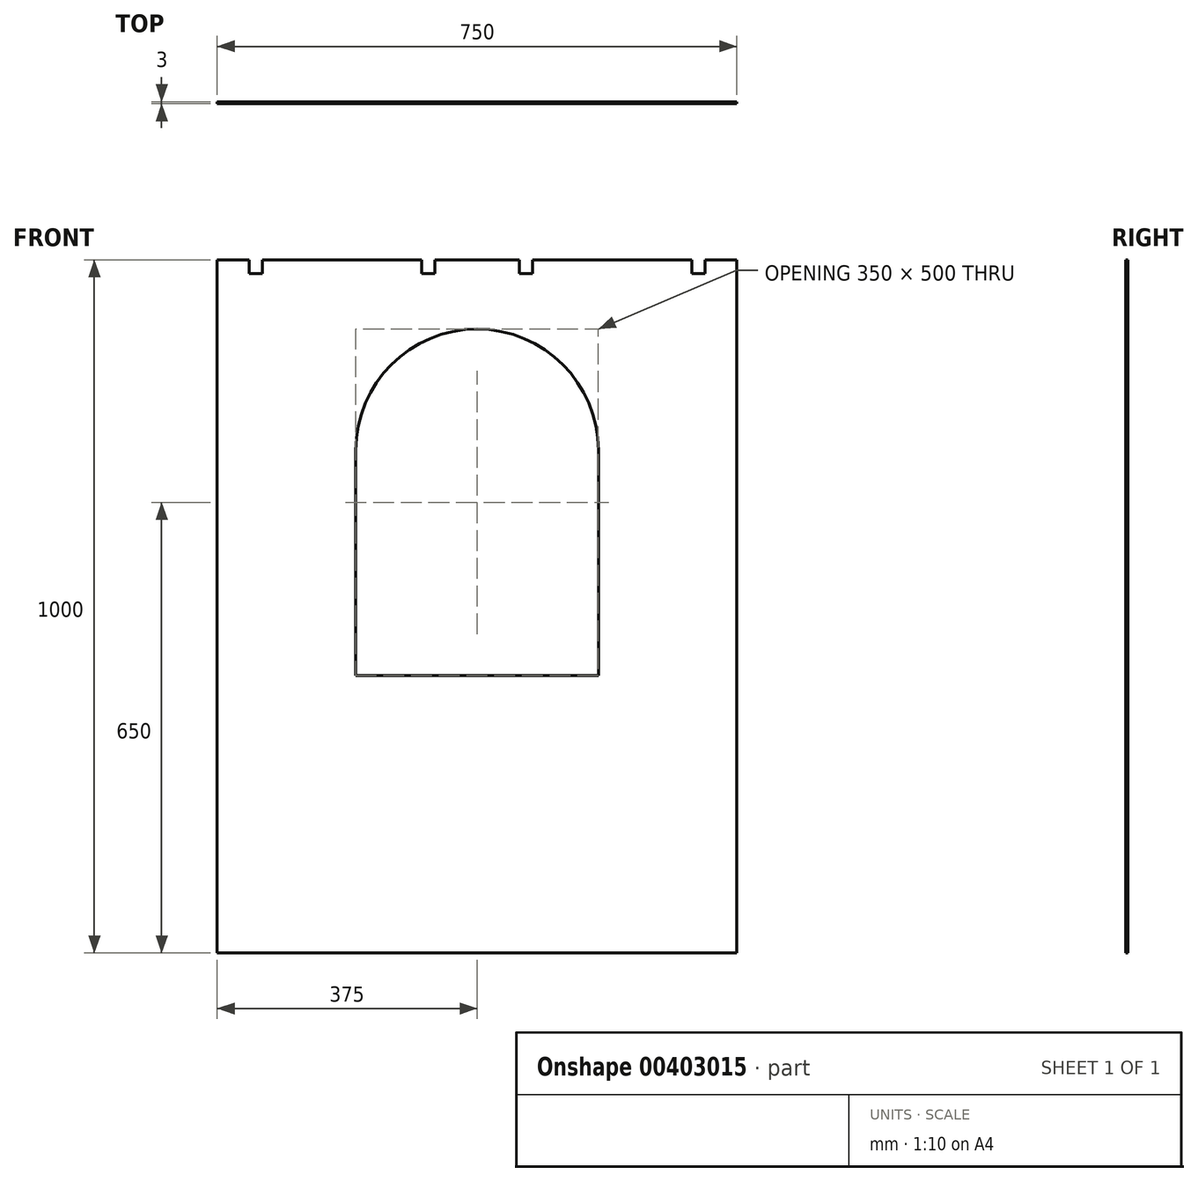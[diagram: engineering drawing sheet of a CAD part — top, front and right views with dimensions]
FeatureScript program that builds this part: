
annotation { "Feature Type Name" : "Feature", "Feature Type Description" : "" }
export const myFeature = defineFeature(function(context is Context, id is Id, definition is map)
    precondition{}
    {
        {
            var Q0;
            Q0=qCreatedBy(makeId("Front.planeOp"),FACE);
            var sketch = newSketch(context, id + "F0", { "sketchPlane" : qUnion([Q0])});
            skLineSegment(sketch, "E0.bottom", {"start": v(0, 0) * mm, "end": v(750, 0) * mm});
            skLineSegment(sketch, "E0.top", {"start": v(0, 1000) * mm, "end": v(46, 1000) * mm});
            skLineSegment(sketch, "E0.left", {"start": v(0, 0) * mm, "end": v(0, 1000) * mm});
            skLineSegment(sketch, "E0.right", {"start": v(750, 0) * mm, "end": v(750, 1000) * mm});
            skLineSegment(sketch, "E1.top", {"start": v(200, 400) * mm, "end": v(550, 400) * mm});
            skLineSegment(sketch, "E1.left", {"start": v(200, 725) * mm, "end": v(200, 400) * mm});
            skLineSegment(sketch, "E1.right", {"start": v(550, 725) * mm, "end": v(550, 400) * mm});
            skArc(sketch, "E2", {"start": v(550, 725) * mm, "mid": v(375, 900) * mm, "end": v(200, 725) * mm});
            skLineSegment(sketch, "E3.top", {"start": v(46, 980) * mm, "end": v(65, 980) * mm});
            skLineSegment(sketch, "E3.left", {"start": v(46, 1000) * mm, "end": v(46, 980) * mm});
            skLineSegment(sketch, "E3.right", {"start": v(65, 1000) * mm, "end": v(65, 980) * mm});
            skLineSegment(sketch, "E4.top", {"start": v(295, 980) * mm, "end": v(314, 980) * mm});
            skLineSegment(sketch, "E4.left", {"start": v(295, 1000) * mm, "end": v(295, 980) * mm});
            skLineSegment(sketch, "E4.right", {"start": v(314, 1000) * mm, "end": v(314, 980) * mm});
            skLineSegment(sketch, "E5.top", {"start": v(685, 980) * mm, "end": v(704, 980) * mm});
            skLineSegment(sketch, "E5.left", {"start": v(685, 1000) * mm, "end": v(685, 980) * mm});
            skLineSegment(sketch, "E5.right", {"start": v(704, 1000) * mm, "end": v(704, 980) * mm});
            skLineSegment(sketch, "E6.trimOffspring", {"start": v(65, 1000) * mm, "end": v(295, 1000) * mm});
            skLineSegment(sketch, "E7.trimOffspring", {"start": v(314, 1000) * mm, "end": v(436, 1000) * mm});
            skLineSegment(sketch, "E8.trimOffspring", {"start": v(704, 1000) * mm, "end": v(750, 1000) * mm});
            skLineSegment(sketch, "E9.top", {"start": v(436, 980) * mm, "end": v(455, 980) * mm});
            skLineSegment(sketch, "E9.left", {"start": v(436, 1000) * mm, "end": v(436, 980) * mm});
            skLineSegment(sketch, "E9.right", {"start": v(455, 1000) * mm, "end": v(455, 980) * mm});
            skLineSegment(sketch, "E10.trimOffspring", {"start": v(455, 1000) * mm, "end": v(685, 1000) * mm});
            skSolve(sketch);
        }
        {
            var Q0;
            Q0=makeQuery(id+"F0.imprint","IMPRINT",FACE,{"disambiguationData":[TD([[makeQuery(id+"F0.imprint","IMPRINT",EDGE,{"derivedFrom":sQuery(id+"F0.wireOp",EDGE,"E0.bottom")}),1.0]])]});
            extrude(context, id + "F1", {"entities" : qUnion([Q0]), "depth" : 3 * mm});
        }
    });
